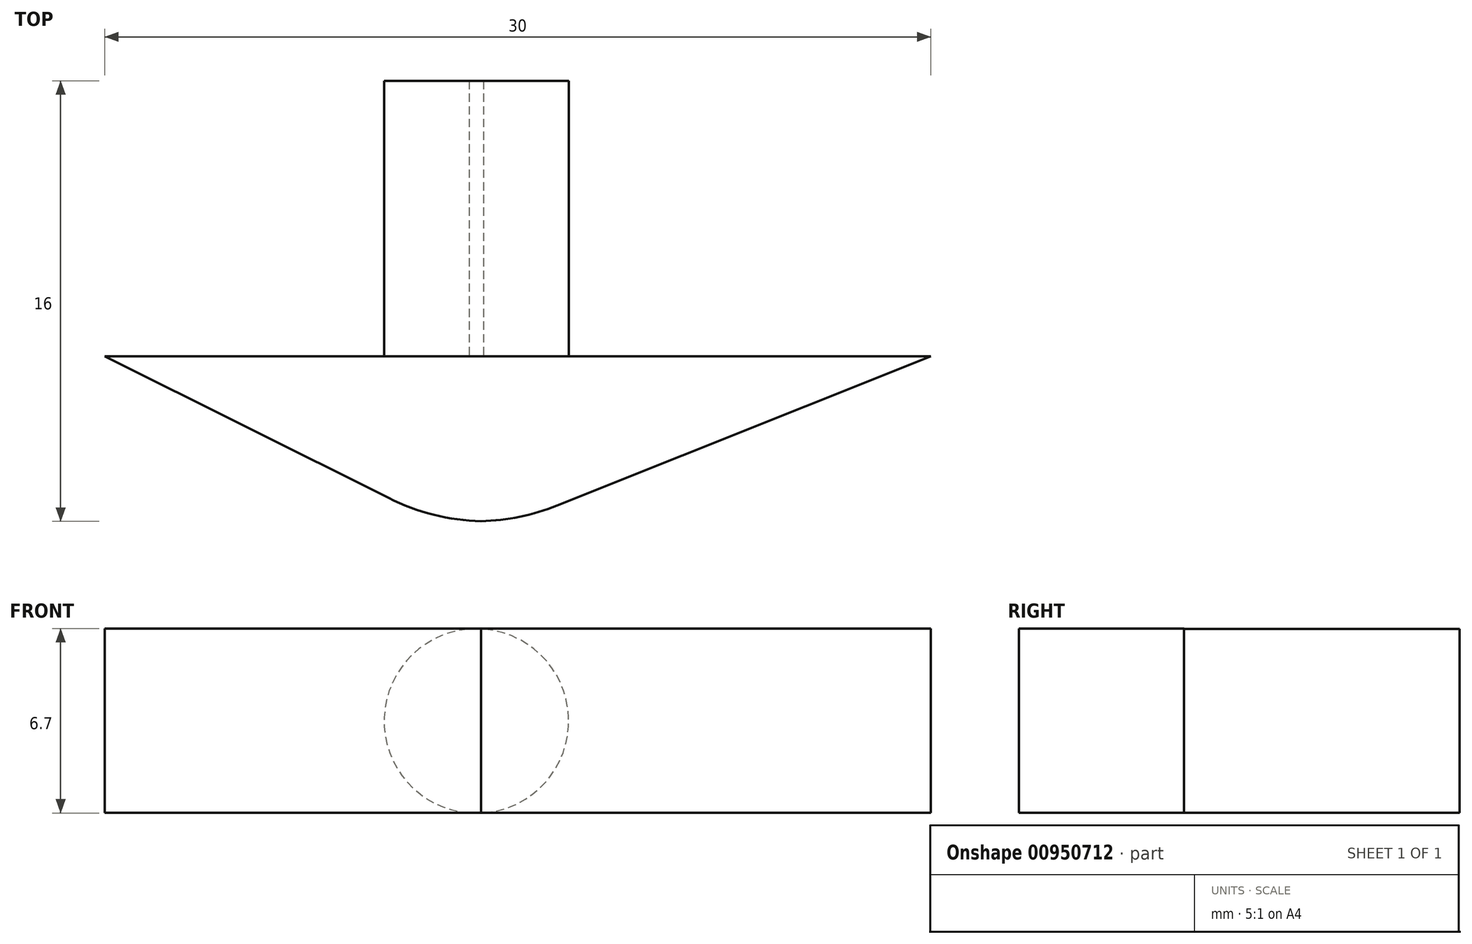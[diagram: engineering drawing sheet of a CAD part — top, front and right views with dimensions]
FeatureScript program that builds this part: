
annotation { "Feature Type Name" : "Feature", "Feature Type Description" : "" }
export const myFeature = defineFeature(function(context is Context, id is Id, definition is map)
    precondition{}
    {
        {
            var Q0;
            Q0=qCreatedBy(makeId("Front.planeOp"),FACE);
            var sketch = newSketch(context, id + "F0", { "sketchPlane" : qUnion([Q0])});
            skLineSegment(sketch, "E0.bottom", {"start": v(-14.7, 3.35) * mm, "end": v(15.3, 3.35) * mm});
            skLineSegment(sketch, "E0.top", {"start": v(-14.7, -3.35) * mm, "end": v(15.3, -3.35) * mm});
            skLineSegment(sketch, "E0.left", {"start": v(-14.7, 3.35) * mm, "end": v(-14.7, -3.35) * mm});
            skLineSegment(sketch, "E0.right", {"start": v(15.3, 3.35) * mm, "end": v(15.3, -3.35) * mm});
            skCircle(sketch, "E1", {"center": v(-1.2, 0) * mm, "radius": 3.35 * mm});
            skSolve(sketch);
        }
        {
            var Q0;
            {var subQ0=sQuery(id+"F0.wireOp",EDGE,"E1");var subQ1=sQuery(id+"F0.wireOp",EDGE,"E0.top");var subQ2=makeQuery(id+"F0.imprint","INTERSECT",VERTEX,{"disambiguationData":[OD(0.0)],"derivedFrom":[subQ1,subQ0]});Q0=makeQuery(id+"F0.imprint","IMPRINT",FACE,{"disambiguationData":[TD([[makeQuery(id+"F0.imprint","IMPRINT",EDGE,{"disambiguationData":[TD([[subQ2,-1.0]])],"derivedFrom":subQ1}),1.0]])]});}
            extrude(context, id + "F1", {"entities" : qUnion([Q0]), "oppositeDirection" : true, "depth" : 10 * mm, "offsetDistance" : 25 * mm});
        }
        {
            var Q0;
            Q0=makeQuery(id+"F0.imprint","IMPRINT",FACE,{"disambiguationData":[TD([[makeQuery(id+"F0.imprint","IMPRINT",EDGE,{"derivedFrom":sQuery(id+"F0.wireOp",EDGE,"E0.bottom")}),-1.0]])]});
            var Q1;
            {var subQ0=sQuery(id+"F0.wireOp",EDGE,"E1");var subQ1=sQuery(id+"F0.wireOp",EDGE,"E0.top");var subQ2=makeQuery(id+"F0.imprint","INTERSECT",VERTEX,{"disambiguationData":[OD(0.0)],"derivedFrom":[subQ1,subQ0]});Q1=makeQuery(id+"F0.imprint","IMPRINT",FACE,{"disambiguationData":[TD([[makeQuery(id+"F0.imprint","IMPRINT",EDGE,{"disambiguationData":[TD([[subQ2,-1.0]])],"derivedFrom":subQ1}),1.0]])]});}
            extrude(context, id + "F2", {"entities" : qUnion([Q0, Q1]), "depth" : 6 * mm, "offsetDistance" : 25 * mm});
        }
        {
            var Q0;
            Q0=makeQuery(id+"F2.opExtrude","CAP_EDGE",EDGE,{"disambiguationData":[OSD([sQuery(id+"F0.wireOp",EDGE,"E0.left")])],"isStart":false});
            chamfer(context, id + "F3", {"entities" : qUnion([Q0]), "chamferType" : ChamferType.TWO_OFFSETS, "width1" : 12 * mm, "oppositeDirection" : false, "width2" : 6 * mm, "tangentPropagation" : true});
        }
        {
            var Q0;
            Q0=makeQuery(id+"F2.opExtrude","CAP_EDGE",EDGE,{"disambiguationData":[OSD([sQuery(id+"F0.wireOp",EDGE,"E0.right")])],"isStart":false});
            chamfer(context, id + "F4", {"entities" : qUnion([Q0]), "chamferType" : ChamferType.TWO_OFFSETS, "width1" : 6 * mm, "oppositeDirection" : false, "width2" : 15 * mm, "tangentPropagation" : true});
        }
        {
            var Q0;
            {var subQ0=sQuery(id+"F0.wireOp",EDGE,"E0.left");Q0=makeQuery(id+"F3.opChamfer","BLEND_EDGE",EDGE,{"blendedFrom":[makeQuery(id+"F2.opExtrude","CAP_EDGE",EDGE,{"disambiguationData":[OSD([subQ0])],"isStart":false}),makeQuery(id+"F2.opExtrude","CAP_FACE",FACE,{"disambiguationData":[OSD([sQuery(id+"F0.wireOp",EDGE,"E0.bottom"),sQuery(id+"F0.wireOp",EDGE,"E0.top"),subQ0,sQuery(id+"F0.wireOp",EDGE,"E0.right")])],"isStart":false})],"blendedInto":[makeQuery(id+"F2.opExtrude","CAP_FACE",FACE,{"disambiguationData":[OSD([sQuery(id+"F0.wireOp",EDGE,"E0.bottom"),sQuery(id+"F0.wireOp",EDGE,"E0.top"),subQ0,sQuery(id+"F0.wireOp",EDGE,"E0.right")])],"isStart":false})]});}
            var Q1;
            {var subQ0=sQuery(id+"F0.wireOp",EDGE,"E0.right");Q1=makeQuery(id+"F4.opChamfer","BLEND_EDGE",EDGE,{"blendedFrom":[makeQuery(id+"F2.opExtrude","CAP_EDGE",EDGE,{"disambiguationData":[OSD([subQ0])],"isStart":false}),makeQuery(id+"F2.opExtrude","CAP_FACE",FACE,{"disambiguationData":[OSD([sQuery(id+"F0.wireOp",EDGE,"E0.bottom"),sQuery(id+"F0.wireOp",EDGE,"E0.top"),sQuery(id+"F0.wireOp",EDGE,"E0.left"),subQ0])],"isStart":false})],"blendedInto":[makeQuery(id+"F2.opExtrude","CAP_FACE",FACE,{"disambiguationData":[OSD([sQuery(id+"F0.wireOp",EDGE,"E0.bottom"),sQuery(id+"F0.wireOp",EDGE,"E0.top"),sQuery(id+"F0.wireOp",EDGE,"E0.left"),subQ0])],"isStart":false})]});}
            fillet(context, id + "F5", {"entities" : qUnion([Q0, Q1]), "radius" : 8 * mm, "tangentPropagation" : true, "allowEdgeOverflow" : false});
        }
    });
